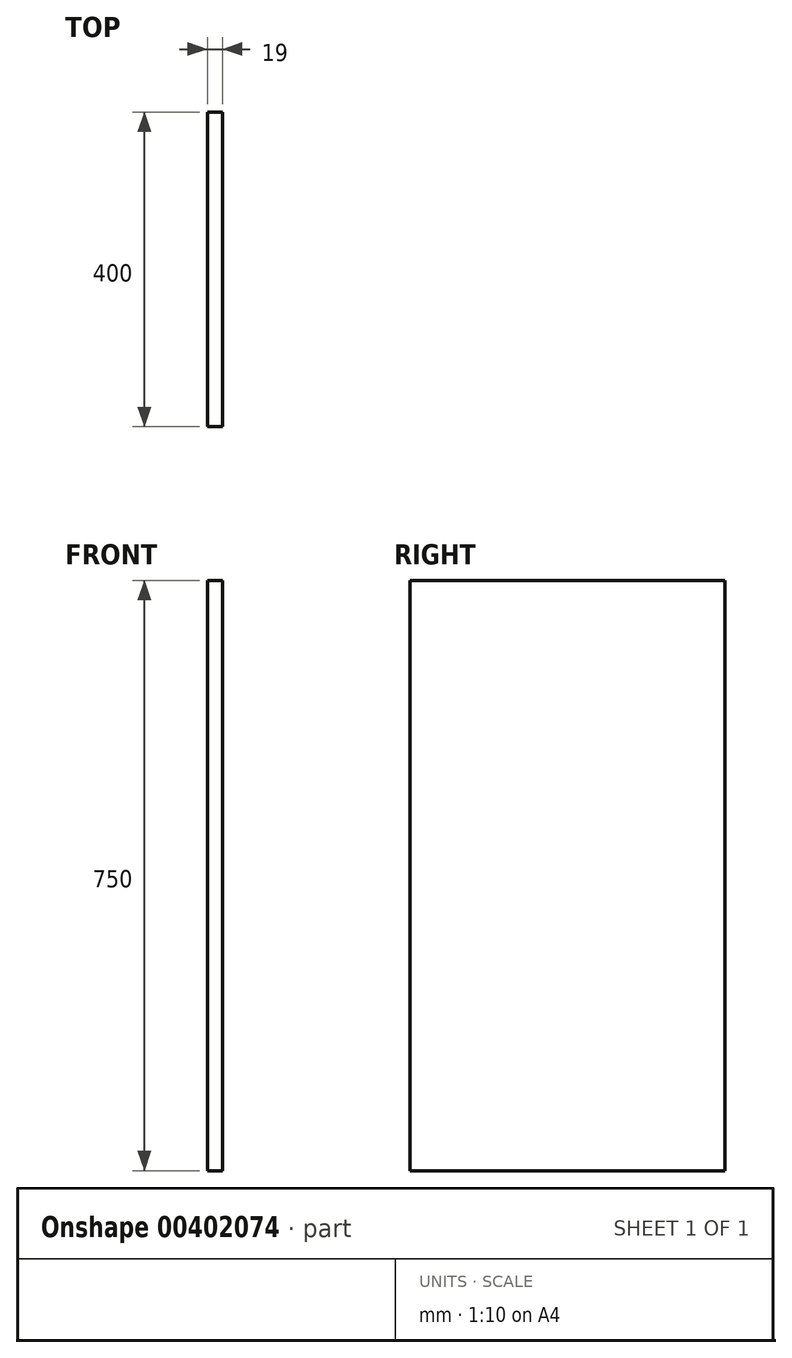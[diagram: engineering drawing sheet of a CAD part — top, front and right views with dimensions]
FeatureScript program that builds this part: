
annotation { "Feature Type Name" : "Feature", "Feature Type Description" : "" }
export const myFeature = defineFeature(function(context is Context, id is Id, definition is map)
    precondition{}
    {
        {
            var Q0;
            Q0=qCreatedBy(makeId("Right.planeOp"),FACE);
            var sketch = newSketch(context, id + "F0", { "sketchPlane" : qUnion([Q0])});
            skLineSegment(sketch, "E0.bottom", {"start": v(0, 0) * mm, "end": v(400, 0) * mm});
            skLineSegment(sketch, "E0.top", {"start": v(0, 750) * mm, "end": v(400, 750) * mm});
            skLineSegment(sketch, "E0.left", {"start": v(0, 0) * mm, "end": v(0, 750) * mm});
            skLineSegment(sketch, "E0.right", {"start": v(400, 0) * mm, "end": v(400, 750) * mm});
            skSolve(sketch);
        }
        {
            var Q0;
            Q0 = qSketchRegion(id + "F0", true);
            extrude(context, id + "F1", {"entities" : qUnion([Q0]), "depth" : 19 * mm});
        }
    });
